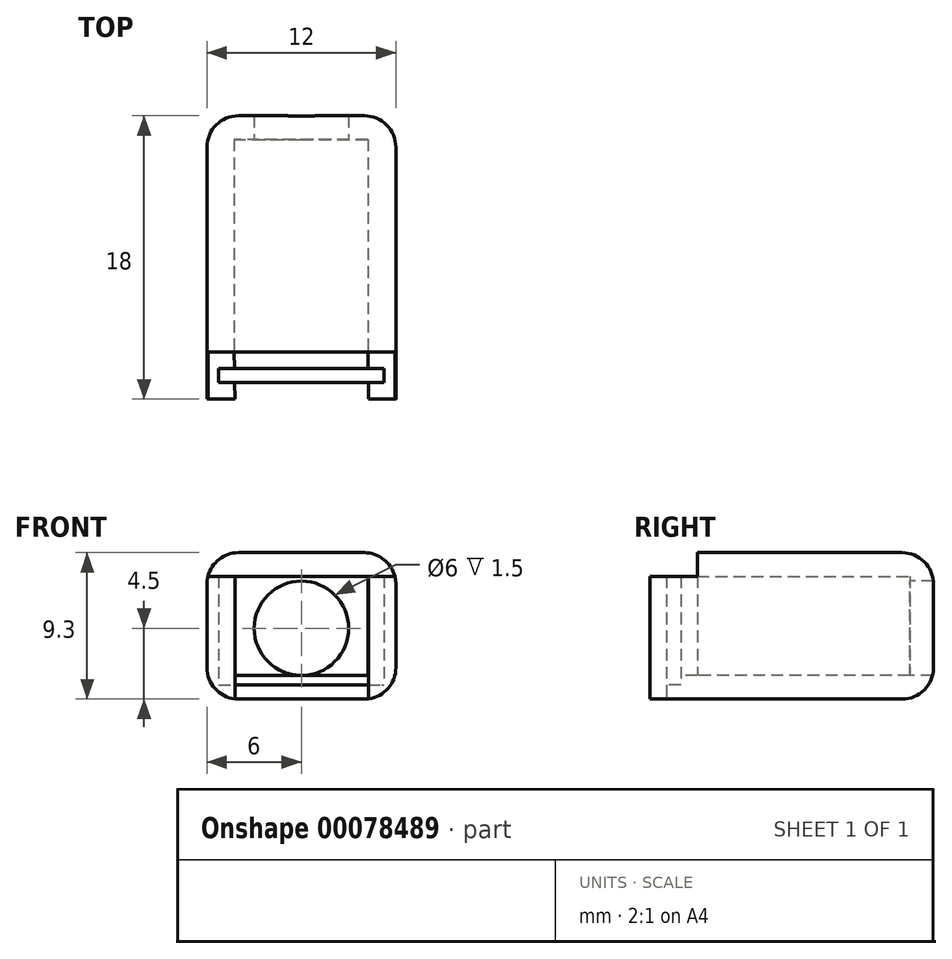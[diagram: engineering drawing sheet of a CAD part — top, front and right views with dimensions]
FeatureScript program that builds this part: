
annotation { "Feature Type Name" : "Feature", "Feature Type Description" : "" }
export const myFeature = defineFeature(function(context is Context, id is Id, definition is map)
    precondition{}
    {
        {
            var Q0;
            Q0=qCreatedBy(makeId("Top.planeOp"),FACE);
            var sketch = newSketch(context, id + "F0", { "sketchPlane" : qUnion([Q0])});
            skPoint(sketch, "E0.rect.middle", {"position": v(0, 0) * mm});
            skLineSegment(sketch, "E1.rect.bottom", {"start": v(-6, -1.5) * mm, "end": v(6, -1.5) * mm});
            skLineSegment(sketch, "E1.rect.top", {"start": v(-6, 1.5) * mm, "end": v(-4.28, 1.5) * mm});
            skLineSegment(sketch, "E1.rect.left", {"start": v(-6, -1.5) * mm, "end": v(-6, 1.5) * mm});
            skLineSegment(sketch, "E1.rect.right", {"start": v(6, -1.5) * mm, "end": v(6, 1.5) * mm});
            skLineSegment(sketch, "E2.rect.bottom", {"start": v(5.25, -0.45) * mm, "end": v(-5.25, -0.45) * mm});
            skLineSegment(sketch, "E2.rect.top", {"start": v(5.25, 0.45) * mm, "end": v(-5.25, 0.45) * mm});
            skLineSegment(sketch, "E2.rect.left", {"start": v(5.25, -0.45) * mm, "end": v(5.25, 0.45) * mm});
            skLineSegment(sketch, "E2.rect.right", {"start": v(-5.25, -0.45) * mm, "end": v(-5.25, 0.45) * mm});
            skLineSegment(sketch, "E3.rect.bottom", {"start": v(-4.22, -1.5) * mm, "end": v(4.28, -1.5) * mm});
            skLineSegment(sketch, "E3.rect.left", {"start": v(-4.22, -1.5) * mm, "end": v(-4.28, 1.5) * mm});
            skLineSegment(sketch, "E3.rect.right", {"start": v(4.28, -1.5) * mm, "end": v(4.22, 1.5) * mm});
            skLineSegment(sketch, "E4.trimOffspring", {"start": v(4.22, 1.5) * mm, "end": v(6, 1.5) * mm});
            skLineSegment(sketch, "E5", {"start": v(-4.28, 1.5) * mm, "end": v(4.22, 1.5) * mm, "construction": true});
            skLineSegment(sketch, "E6.bottom", {"start": v(6, 1.5) * mm, "end": v(-6, 1.5) * mm});
            skLineSegment(sketch, "E7.bottom", {"start": v(4.22, 1.5) * mm, "end": v(-6, 1.5) * mm});
            skLineSegment(sketch, "E8.bottom", {"start": v(-6, 1.5) * mm, "end": v(6, 1.5) * mm});
            skLineSegment(sketch, "E8.top", {"start": v(-6, 16.5) * mm, "end": v(6, 16.5) * mm});
            skLineSegment(sketch, "E8.left", {"start": v(-6, 1.5) * mm, "end": v(-6, 16.5) * mm});
            skLineSegment(sketch, "E8.right", {"start": v(6, 1.5) * mm, "end": v(6, 16.5) * mm});
            skLineSegment(sketch, "E9", {"start": v(-4.28, 1.5) * mm, "end": v(-4.28, 16.5) * mm});
            skLineSegment(sketch, "E10", {"start": v(4.22, 1.5) * mm, "end": v(4.22, 16.5) * mm});
            skLineSegment(sketch, "E11", {"start": v(6, 15) * mm, "end": v(-6, 15) * mm});
            skSolve(sketch);
        }
        {
            var Q0;
            {var subQ0=sQuery(id+"F0.wireOp",EDGE,"E6.right");Q0=makeQuery(id+"F0.imprint","IMPRINT",FACE,{"disambiguationData":[TD([[makeQuery(id+"F0.imprint","IMPRINT",EDGE,{"derivedFrom":subQ0}),-1.0]])]});}
            var Q1;
            Q1=makeQuery(id+"F0.imprint","IMPRINT",FACE,{"disambiguationData":[TD([[makeQuery(id+"F0.imprint","IMPRINT",EDGE,{"derivedFrom":sQuery(id+"F0.wireOp",EDGE,"E7.bottom")}),-1.0]])]});
            var Q2;
            {var subQ5=sQuery(id+"F0.wireOp",EDGE,"E7.bottom");Q2=makeQuery(id+"F0.imprint","IMPRINT",FACE,{"disambiguationData":[TD([[makeQuery(id+"F0.imprint","IMPRINT",EDGE,{"derivedFrom":subQ5}),1.0]])]});}
            var Q3;
            {var subQ8=sQuery(id+"F0.wireOp",EDGE,"E1.rect.right");Q3=makeQuery(id+"F0.imprint","IMPRINT",FACE,{"disambiguationData":[TD([[makeQuery(id+"F0.imprint","IMPRINT",EDGE,{"derivedFrom":subQ8}),1.0]])]});}
            var Q4;
            {var subQ5=sQuery(id+"F0.wireOp",EDGE,"E3.rect.bottom");Q4=makeQuery(id+"F0.imprint","IMPRINT",FACE,{"disambiguationData":[TD([[makeQuery(id+"F0.imprint","IMPRINT",EDGE,{"derivedFrom":subQ5}),1.0]])]});}
            var Q5;
            {var subQ4=sQuery(id+"F0.wireOp",EDGE,"E1.rect.left");Q5=makeQuery(id+"F0.imprint","IMPRINT",FACE,{"disambiguationData":[TD([[makeQuery(id+"F0.imprint","IMPRINT",EDGE,{"derivedFrom":subQ4}),-1.0]])]});}
            var Q6;
            {var subQ0=sQuery(id+"F0.wireOp",EDGE,"E6.left");Q6=makeQuery(id+"F0.imprint","IMPRINT",FACE,{"disambiguationData":[TD([[makeQuery(id+"F0.imprint","IMPRINT",EDGE,{"derivedFrom":subQ0}),1.0]])]});}
            var Q7;
            {var subQ0=sQuery(id+"F0.wireOp",EDGE,"E3.rect.right");var subQ1=sQuery(id+"F0.wireOp",EDGE,"E2.rect.bottom");var subQ2=makeQuery(id+"F0.imprint","INTERSECT",VERTEX,{"derivedFrom":[subQ1,subQ0]});Q7=makeQuery(id+"F0.imprint","IMPRINT",FACE,{"disambiguationData":[TD([[makeQuery(id+"F0.imprint","IMPRINT",EDGE,{"disambiguationData":[TD([[subQ2,-1.0]])],"derivedFrom":subQ1}),-1.0]])]});}
            var Q8;
            {var subQ0=sQuery(id+"F0.wireOp",EDGE,"E2.rect.right");Q8=makeQuery(id+"F0.imprint","IMPRINT",FACE,{"disambiguationData":[TD([[makeQuery(id+"F0.imprint","IMPRINT",EDGE,{"derivedFrom":subQ0}),-1.0]])]});}
            var Q9;
            {var subQ0=sQuery(id+"F0.wireOp",EDGE,"E2.rect.left");Q9=makeQuery(id+"F0.imprint","IMPRINT",FACE,{"disambiguationData":[TD([[makeQuery(id+"F0.imprint","IMPRINT",EDGE,{"derivedFrom":subQ0}),1.0]])]});}
            var Q10;
            {var subQ0=sQuery(id+"F0.wireOp",EDGE,"E8.left");var subQ5=sQuery(id+"F0.wireOp",EDGE,"E11");var subQ6=makeQuery(id+"F0.imprint","INTERSECT",VERTEX,{"derivedFrom":[subQ0,subQ5]});Q10=makeQuery(id+"F0.imprint","IMPRINT",FACE,{"disambiguationData":[TD([[makeQuery(id+"F0.imprint","IMPRINT",EDGE,{"disambiguationData":[TD([[subQ6,1.0]])],"derivedFrom":subQ5}),1.0]])]});}
            var Q11;
            {var subQ0=sQuery(id+"F0.wireOp",EDGE,"E8.left");var subQ1=sQuery(id+"F0.wireOp",EDGE,"E8.top");var subQ2=makeQuery(id+"F0.imprint","INTERSECT",VERTEX,{"derivedFrom":[subQ1,subQ0]});Q11=makeQuery(id+"F0.imprint","IMPRINT",FACE,{"disambiguationData":[TD([[makeQuery(id+"F0.imprint","IMPRINT",EDGE,{"disambiguationData":[TD([[subQ2,-1.0]])],"derivedFrom":subQ1}),-1.0]])]});}
            var Q12;
            {var subQ0=sQuery(id+"F0.wireOp",EDGE,"E9");var subQ1=sQuery(id+"F0.wireOp",EDGE,"E8.top");var subQ2=makeQuery(id+"F0.imprint","INTERSECT",VERTEX,{"derivedFrom":[subQ1,subQ0]});Q12=makeQuery(id+"F0.imprint","IMPRINT",FACE,{"disambiguationData":[TD([[makeQuery(id+"F0.imprint","IMPRINT",EDGE,{"disambiguationData":[TD([[subQ2,-1.0]])],"derivedFrom":subQ1}),-1.0]])]});}
            var Q13;
            {var subQ0=sQuery(id+"F0.wireOp",EDGE,"E8.right");var subQ1=sQuery(id+"F0.wireOp",EDGE,"E8.top");var subQ2=makeQuery(id+"F0.imprint","INTERSECT",VERTEX,{"derivedFrom":[subQ1,subQ0]});Q13=makeQuery(id+"F0.imprint","IMPRINT",FACE,{"disambiguationData":[TD([[makeQuery(id+"F0.imprint","IMPRINT",EDGE,{"disambiguationData":[TD([[subQ2,1.0]])],"derivedFrom":subQ1}),-1.0]])]});}
            var Q14;
            {var subQ0=sQuery(id+"F0.wireOp",EDGE,"E8.right");var subQ5=sQuery(id+"F0.wireOp",EDGE,"E11");var subQ6=makeQuery(id+"F0.imprint","INTERSECT",VERTEX,{"derivedFrom":[subQ0,subQ5]});Q14=makeQuery(id+"F0.imprint","IMPRINT",FACE,{"disambiguationData":[TD([[makeQuery(id+"F0.imprint","IMPRINT",EDGE,{"disambiguationData":[TD([[subQ6,-1.0]])],"derivedFrom":subQ5}),1.0]])]});}
            var Q15;
            {var subQ0=sQuery(id+"F0.wireOp",EDGE,"E3.rect.right");var subQ1=sQuery(id+"F0.wireOp",EDGE,"E2.rect.top");var subQ2=makeQuery(id+"F0.imprint","INTERSECT",VERTEX,{"derivedFrom":[subQ1,subQ0]});Q15=makeQuery(id+"F0.imprint","IMPRINT",FACE,{"disambiguationData":[TD([[makeQuery(id+"F0.imprint","IMPRINT",EDGE,{"disambiguationData":[TD([[subQ2,-1.0]])],"derivedFrom":subQ1}),-1.0]])]});}
            var Q16;
            {var subQ0=sQuery(id+"F0.wireOp",EDGE,"E9");var subQ5=sQuery(id+"F0.wireOp",EDGE,"E11");var subQ6=makeQuery(id+"F0.imprint","INTERSECT",VERTEX,{"derivedFrom":[subQ0,subQ5]});Q16=makeQuery(id+"F0.imprint","IMPRINT",FACE,{"disambiguationData":[TD([[makeQuery(id+"F0.imprint","IMPRINT",EDGE,{"disambiguationData":[TD([[subQ6,1.0]])],"derivedFrom":subQ5}),1.0]])]});}
            extrude(context, id + "F1", {"entities" : qUnion([Q0, Q1, Q2, Q3, Q4, Q5, Q6, Q7, Q8, Q9, Q10, Q11, Q12, Q13, Q14, Q15, Q16]), "depth" : 0.9 * mm});
        }
        {
            var Q0;
            {var subQ0=sQuery(id+"F0.wireOp",EDGE,"E6.left");Q0=makeQuery(id+"F0.imprint","IMPRINT",FACE,{"disambiguationData":[TD([[makeQuery(id+"F0.imprint","IMPRINT",EDGE,{"derivedFrom":subQ0}),1.0]])]});}
            var Q1;
            {var subQ0=sQuery(id+"F0.wireOp",EDGE,"E6.right");Q1=makeQuery(id+"F0.imprint","IMPRINT",FACE,{"disambiguationData":[TD([[makeQuery(id+"F0.imprint","IMPRINT",EDGE,{"derivedFrom":subQ0}),-1.0]])]});}
            var Q2;
            {var subQ5=sQuery(id+"F0.wireOp",EDGE,"E3.rect.bottom");Q2=makeQuery(id+"F0.imprint","IMPRINT",FACE,{"disambiguationData":[TD([[makeQuery(id+"F0.imprint","IMPRINT",EDGE,{"derivedFrom":subQ5}),1.0]])]});}
            var Q3;
            {var subQ4=sQuery(id+"F0.wireOp",EDGE,"E1.rect.left");Q3=makeQuery(id+"F0.imprint","IMPRINT",FACE,{"disambiguationData":[TD([[makeQuery(id+"F0.imprint","IMPRINT",EDGE,{"derivedFrom":subQ4}),-1.0]])]});}
            var Q4;
            {var subQ8=sQuery(id+"F0.wireOp",EDGE,"E1.rect.right");Q4=makeQuery(id+"F0.imprint","IMPRINT",FACE,{"disambiguationData":[TD([[makeQuery(id+"F0.imprint","IMPRINT",EDGE,{"derivedFrom":subQ8}),1.0]])]});}
            var Q5;
            {var subQ5=sQuery(id+"F0.wireOp",EDGE,"E7.bottom");Q5=makeQuery(id+"F0.imprint","IMPRINT",FACE,{"disambiguationData":[TD([[makeQuery(id+"F0.imprint","IMPRINT",EDGE,{"derivedFrom":subQ5}),1.0]])]});}
            var Q6;
            {var subQ0=sQuery(id+"F0.wireOp",EDGE,"E8.right");var subQ5=sQuery(id+"F0.wireOp",EDGE,"E11");var subQ6=makeQuery(id+"F0.imprint","INTERSECT",VERTEX,{"derivedFrom":[subQ0,subQ5]});Q6=makeQuery(id+"F0.imprint","IMPRINT",FACE,{"disambiguationData":[TD([[makeQuery(id+"F0.imprint","IMPRINT",EDGE,{"disambiguationData":[TD([[subQ6,-1.0]])],"derivedFrom":subQ5}),1.0]])]});}
            var Q7;
            {var subQ0=sQuery(id+"F0.wireOp",EDGE,"E3.rect.right");var subQ1=sQuery(id+"F0.wireOp",EDGE,"E2.rect.top");var subQ2=makeQuery(id+"F0.imprint","INTERSECT",VERTEX,{"derivedFrom":[subQ1,subQ0]});Q7=makeQuery(id+"F0.imprint","IMPRINT",FACE,{"disambiguationData":[TD([[makeQuery(id+"F0.imprint","IMPRINT",EDGE,{"disambiguationData":[TD([[subQ2,-1.0]])],"derivedFrom":subQ1}),-1.0]])]});}
            var Q8;
            {var subQ0=sQuery(id+"F0.wireOp",EDGE,"E9");var subQ5=sQuery(id+"F0.wireOp",EDGE,"E11");var subQ6=makeQuery(id+"F0.imprint","INTERSECT",VERTEX,{"derivedFrom":[subQ0,subQ5]});Q8=makeQuery(id+"F0.imprint","IMPRINT",FACE,{"disambiguationData":[TD([[makeQuery(id+"F0.imprint","IMPRINT",EDGE,{"disambiguationData":[TD([[subQ6,1.0]])],"derivedFrom":subQ5}),1.0]])]});}
            var Q9;
            {var subQ0=sQuery(id+"F0.wireOp",EDGE,"E8.left");var subQ5=sQuery(id+"F0.wireOp",EDGE,"E11");var subQ6=makeQuery(id+"F0.imprint","INTERSECT",VERTEX,{"derivedFrom":[subQ0,subQ5]});Q9=makeQuery(id+"F0.imprint","IMPRINT",FACE,{"disambiguationData":[TD([[makeQuery(id+"F0.imprint","IMPRINT",EDGE,{"disambiguationData":[TD([[subQ6,1.0]])],"derivedFrom":subQ5}),1.0]])]});}
            var Q10;
            {var subQ0=sQuery(id+"F0.wireOp",EDGE,"E8.left");var subQ1=sQuery(id+"F0.wireOp",EDGE,"E8.top");var subQ2=makeQuery(id+"F0.imprint","INTERSECT",VERTEX,{"derivedFrom":[subQ1,subQ0]});Q10=makeQuery(id+"F0.imprint","IMPRINT",FACE,{"disambiguationData":[TD([[makeQuery(id+"F0.imprint","IMPRINT",EDGE,{"disambiguationData":[TD([[subQ2,-1.0]])],"derivedFrom":subQ1}),-1.0]])]});}
            var Q11;
            {var subQ0=sQuery(id+"F0.wireOp",EDGE,"E9");var subQ1=sQuery(id+"F0.wireOp",EDGE,"E8.top");var subQ2=makeQuery(id+"F0.imprint","INTERSECT",VERTEX,{"derivedFrom":[subQ1,subQ0]});Q11=makeQuery(id+"F0.imprint","IMPRINT",FACE,{"disambiguationData":[TD([[makeQuery(id+"F0.imprint","IMPRINT",EDGE,{"disambiguationData":[TD([[subQ2,-1.0]])],"derivedFrom":subQ1}),-1.0]])]});}
            var Q12;
            {var subQ0=sQuery(id+"F0.wireOp",EDGE,"E8.right");var subQ1=sQuery(id+"F0.wireOp",EDGE,"E8.top");var subQ2=makeQuery(id+"F0.imprint","INTERSECT",VERTEX,{"derivedFrom":[subQ1,subQ0]});Q12=makeQuery(id+"F0.imprint","IMPRINT",FACE,{"disambiguationData":[TD([[makeQuery(id+"F0.imprint","IMPRINT",EDGE,{"disambiguationData":[TD([[subQ2,1.0]])],"derivedFrom":subQ1}),-1.0]])]});}
            extrude(context, id + "F2", {"entities" : qUnion([Q0, Q1, Q2, Q3, Q4, Q5, Q6, Q7, Q8, Q9, Q10, Q11, Q12]), "operationType" : NewBodyOperationType.ADD, "depth" : 1.5 * mm});
        }
        {
            var Q0;
            {var subQ9=sQuery(id+"F0.wireOp",EDGE,"E1.rect.top");Q0=makeQuery(id+"F0.imprint","IMPRINT",FACE,{"disambiguationData":[TD([[makeQuery(id+"F0.imprint","IMPRINT",EDGE,{"derivedFrom":subQ9}),-1.0]])]});}
            var Q1;
            {var subQ4=sQuery(id+"F0.wireOp",EDGE,"E1.rect.right");Q1=makeQuery(id+"F0.imprint","IMPRINT",FACE,{"disambiguationData":[TD([[makeQuery(id+"F0.imprint","IMPRINT",EDGE,{"derivedFrom":subQ4}),1.0]])]});}
            var Q2;
            {var subQ4=sQuery(id+"F0.wireOp",EDGE,"E1.rect.left");Q2=makeQuery(id+"F0.imprint","IMPRINT",FACE,{"disambiguationData":[TD([[makeQuery(id+"F0.imprint","IMPRINT",EDGE,{"derivedFrom":subQ4}),-1.0]])]});}
            var Q3;
            {var subQ0=sQuery(id+"F0.wireOp",EDGE,"E6.right");Q3=makeQuery(id+"F0.imprint","IMPRINT",FACE,{"disambiguationData":[TD([[makeQuery(id+"F0.imprint","IMPRINT",EDGE,{"derivedFrom":subQ0}),-1.0]])]});}
            var Q4;
            {var subQ0=sQuery(id+"F0.wireOp",EDGE,"E6.left");Q4=makeQuery(id+"F0.imprint","IMPRINT",FACE,{"disambiguationData":[TD([[makeQuery(id+"F0.imprint","IMPRINT",EDGE,{"derivedFrom":subQ0}),1.0]])]});}
            var Q5;
            {var subQ0=sQuery(id+"F0.wireOp",EDGE,"E8.left");var subQ5=sQuery(id+"F0.wireOp",EDGE,"E11");var subQ6=makeQuery(id+"F0.imprint","INTERSECT",VERTEX,{"derivedFrom":[subQ0,subQ5]});Q5=makeQuery(id+"F0.imprint","IMPRINT",FACE,{"disambiguationData":[TD([[makeQuery(id+"F0.imprint","IMPRINT",EDGE,{"disambiguationData":[TD([[subQ6,1.0]])],"derivedFrom":subQ5}),1.0]])]});}
            var Q6;
            {var subQ0=sQuery(id+"F0.wireOp",EDGE,"E8.right");var subQ5=sQuery(id+"F0.wireOp",EDGE,"E11");var subQ6=makeQuery(id+"F0.imprint","INTERSECT",VERTEX,{"derivedFrom":[subQ0,subQ5]});Q6=makeQuery(id+"F0.imprint","IMPRINT",FACE,{"disambiguationData":[TD([[makeQuery(id+"F0.imprint","IMPRINT",EDGE,{"disambiguationData":[TD([[subQ6,-1.0]])],"derivedFrom":subQ5}),1.0]])]});}
            var Q7;
            {var subQ0=sQuery(id+"F0.wireOp",EDGE,"E8.left");var subQ1=sQuery(id+"F0.wireOp",EDGE,"E8.top");var subQ2=makeQuery(id+"F0.imprint","INTERSECT",VERTEX,{"derivedFrom":[subQ1,subQ0]});Q7=makeQuery(id+"F0.imprint","IMPRINT",FACE,{"disambiguationData":[TD([[makeQuery(id+"F0.imprint","IMPRINT",EDGE,{"disambiguationData":[TD([[subQ2,-1.0]])],"derivedFrom":subQ1}),-1.0]])]});}
            var Q8;
            {var subQ0=sQuery(id+"F0.wireOp",EDGE,"E9");var subQ1=sQuery(id+"F0.wireOp",EDGE,"E8.top");var subQ2=makeQuery(id+"F0.imprint","INTERSECT",VERTEX,{"derivedFrom":[subQ1,subQ0]});Q8=makeQuery(id+"F0.imprint","IMPRINT",FACE,{"disambiguationData":[TD([[makeQuery(id+"F0.imprint","IMPRINT",EDGE,{"disambiguationData":[TD([[subQ2,-1.0]])],"derivedFrom":subQ1}),-1.0]])]});}
            var Q9;
            {var subQ0=sQuery(id+"F0.wireOp",EDGE,"E8.right");var subQ1=sQuery(id+"F0.wireOp",EDGE,"E8.top");var subQ2=makeQuery(id+"F0.imprint","INTERSECT",VERTEX,{"derivedFrom":[subQ1,subQ0]});Q9=makeQuery(id+"F0.imprint","IMPRINT",FACE,{"disambiguationData":[TD([[makeQuery(id+"F0.imprint","IMPRINT",EDGE,{"disambiguationData":[TD([[subQ2,1.0]])],"derivedFrom":subQ1}),-1.0]])]});}
            extrude(context, id + "F3", {"entities" : qUnion([Q0, Q1, Q2, Q3, Q4, Q5, Q6, Q7, Q8, Q9]), "operationType" : NewBodyOperationType.ADD, "depth" : 7.8 * mm});
        }
        {
            var Q0;
            Q0=makeQuery(id+"F3.opExtrude","CAP_FACE",FACE,{"disambiguationData":[OSD([sQuery(id+"F0.wireOp",EDGE,"E1.rect.bottom"),sQuery(id+"F0.wireOp",EDGE,"E1.rect.left"),sQuery(id+"F0.wireOp",EDGE,"E1.rect.right"),sQuery(id+"F0.wireOp",EDGE,"E2.rect.bottom"),sQuery(id+"F0.wireOp",EDGE,"E2.rect.top"),sQuery(id+"F0.wireOp",EDGE,"E2.rect.left"),sQuery(id+"F0.wireOp",EDGE,"E2.rect.right"),sQuery(id+"F0.wireOp",EDGE,"E3.rect.left"),sQuery(id+"F0.wireOp",EDGE,"E3.rect.right"),sQuery(id+"F0.wireOp",EDGE,"E8.top"),sQuery(id+"F0.wireOp",EDGE,"E8.left"),sQuery(id+"F0.wireOp",EDGE,"E8.right"),sQuery(id+"F0.wireOp",EDGE,"E9"),sQuery(id+"F0.wireOp",EDGE,"E10"),sQuery(id+"F0.wireOp",EDGE,"E11")])],"isStart":false});
            cPlane(context, id + "F4", {"entities" : qUnion([Q0]), "cplaneType" : CPlaneType.OFFSET, "offset" : 0 * mm, "width" : 150 * mm, "height" : 150 * mm});
        }
        {
            var Q0;
            Q0=qCreatedBy(id+"F4.planeOp",FACE);
            var sketch = newSketch(context, id + "F5", { "sketchPlane" : qUnion([Q0])});
            skLineSegment(sketch, "E12.bottom", {"start": v(6, 1.5) * mm, "end": v(-6, 1.5) * mm});
            skLineSegment(sketch, "E12.top", {"start": v(6, -1.5) * mm, "end": v(-6, -1.5) * mm});
            skLineSegment(sketch, "E12.left", {"start": v(6, 1.5) * mm, "end": v(6, -1.5) * mm});
            skLineSegment(sketch, "E12.right", {"start": v(-6, 1.5) * mm, "end": v(-6, -1.5) * mm});
            skPoint(sketch, "E12.middle", {"position": v(0, 0) * mm});
            skLineSegment(sketch, "E13.top", {"start": v(6, 16.5) * mm, "end": v(-6, 16.5) * mm});
            skLineSegment(sketch, "E13.left", {"start": v(6, 1.5) * mm, "end": v(6, 16.5) * mm});
            skLineSegment(sketch, "E13.right", {"start": v(-6, 1.5) * mm, "end": v(-6, 16.5) * mm});
            skSolve(sketch);
        }
        {
            var Q0;
            Q0=makeQuery(id+"F5.imprint","IMPRINT",FACE,{"disambiguationData":[TD([[makeQuery(id+"F5.imprint","IMPRINT",EDGE,{"derivedFrom":sQuery(id+"F5.wireOp",EDGE,"E12.bottom")}),-1.0]])]});
            extrude(context, id + "F6", {"entities" : qUnion([Q0]), "operationType" : NewBodyOperationType.ADD, "depth" : 1.5 * mm});
        }
        {
            var Q0;
            Q0=qCreatedBy(makeId("Front.planeOp"),FACE);
            var sketch = newSketch(context, id + "F7", { "sketchPlane" : qUnion([Q0])});
            skLineSegment(sketch, "E14", {"start": v(0, 0) * mm, "end": v(0, 9) * mm, "construction": true});
            skCircle(sketch, "E15", {"center": v(0, 4.5) * mm, "radius": 3 * mm});
            skSolve(sketch);
        }
        {
            var Q0;
            Q0=qSketchRegion(id+"F7",true);
            extrude(context, id + "F8", {"entities" : qUnion([Q0]), "operationType" : NewBodyOperationType.REMOVE, "endBound" : BoundingType.THROUGH_ALL, "oppositeDirection" : true, "depth" : 25 * mm});
        }
        {
            var Q0;
            {var subQ0=sQuery(id+"F0.wireOp",EDGE,"E8.right");var subQ1=sQuery(id+"F0.wireOp",EDGE,"E8.top");Q0=makeQuery(id+"F6.boolean.opBoolean","MERGE",EDGE,{"derivedFrom":[makeQuery(id+"F3.boolean.opBoolean","MERGE",EDGE,{"derivedFrom":[makeQuery(id+"F2.boolean.opBoolean","MERGE",EDGE,{"derivedFrom":[makeQuery(id+"F1.opExtrude","SWEPT_EDGE",EDGE,{"disambiguationData":[OSD([subQ1,subQ0])]}),makeQuery(id+"F2.opExtrude","SWEPT_EDGE",EDGE,{"disambiguationData":[OSD([subQ1,subQ0])]})]}),makeQuery(id+"F3.opExtrude","SWEPT_EDGE",EDGE,{"disambiguationData":[OSD([subQ1,subQ0])]})]}),makeQuery(id+"F6.opExtrude","SWEPT_EDGE",EDGE,{"disambiguationData":[OSD([sQuery(id+"F5.wireOp",EDGE,"E13.top"),sQuery(id+"F5.wireOp",EDGE,"E13.left")])]})]});}
            var Q1;
            Q1=makeQuery(id+"F6.opExtrude","CAP_EDGE",EDGE,{"disambiguationData":[OSD([sQuery(id+"F5.wireOp",EDGE,"E13.top")])],"isStart":false});
            var Q2;
            Q2=makeQuery(id+"F6.opExtrude","CAP_EDGE",EDGE,{"disambiguationData":[OSD([sQuery(id+"F5.wireOp",EDGE,"E13.left")])],"isStart":false});
            var Q3;
            Q3=makeQuery(id+"F1.opExtrude","CAP_EDGE",EDGE,{"disambiguationData":[OSD([sQuery(id+"F0.wireOp",EDGE,"E1.rect.right"),sQuery(id+"F0.wireOp",EDGE,"E8.right")])],"isStart":true});
            var Q4;
            Q4=makeQuery(id+"F1.opExtrude","CAP_EDGE",EDGE,{"disambiguationData":[OSD([sQuery(id+"F0.wireOp",EDGE,"E8.top")])],"isStart":true});
            var Q5;
            Q5=makeQuery(id+"F1.opExtrude","CAP_EDGE",EDGE,{"disambiguationData":[OSD([sQuery(id+"F0.wireOp",EDGE,"E1.rect.left"),sQuery(id+"F0.wireOp",EDGE,"E8.left")])],"isStart":true});
            var Q6;
            {var subQ0=sQuery(id+"F0.wireOp",EDGE,"E8.left");var subQ1=sQuery(id+"F0.wireOp",EDGE,"E8.top");Q6=makeQuery(id+"F6.boolean.opBoolean","MERGE",EDGE,{"derivedFrom":[makeQuery(id+"F3.boolean.opBoolean","MERGE",EDGE,{"derivedFrom":[makeQuery(id+"F2.boolean.opBoolean","MERGE",EDGE,{"derivedFrom":[makeQuery(id+"F1.opExtrude","SWEPT_EDGE",EDGE,{"disambiguationData":[OSD([subQ1,subQ0])]}),makeQuery(id+"F2.opExtrude","SWEPT_EDGE",EDGE,{"disambiguationData":[OSD([subQ1,subQ0])]})]}),makeQuery(id+"F3.opExtrude","SWEPT_EDGE",EDGE,{"disambiguationData":[OSD([subQ1,subQ0])]})]}),makeQuery(id+"F6.opExtrude","SWEPT_EDGE",EDGE,{"disambiguationData":[OSD([sQuery(id+"F5.wireOp",EDGE,"E13.top"),sQuery(id+"F5.wireOp",EDGE,"E13.right")])]})]});}
            var Q7;
            Q7=makeQuery(id+"F6.opExtrude","CAP_EDGE",EDGE,{"disambiguationData":[OSD([sQuery(id+"F5.wireOp",EDGE,"E13.right")])],"isStart":false});
            fillet(context, id + "F9", {"entities" : qUnion([Q0, Q1, Q2, Q3, Q4, Q5, Q6, Q7]), "radius" : 2 * mm, "tangentPropagation" : true, "allowEdgeOverflow" : false});
        }
    });
